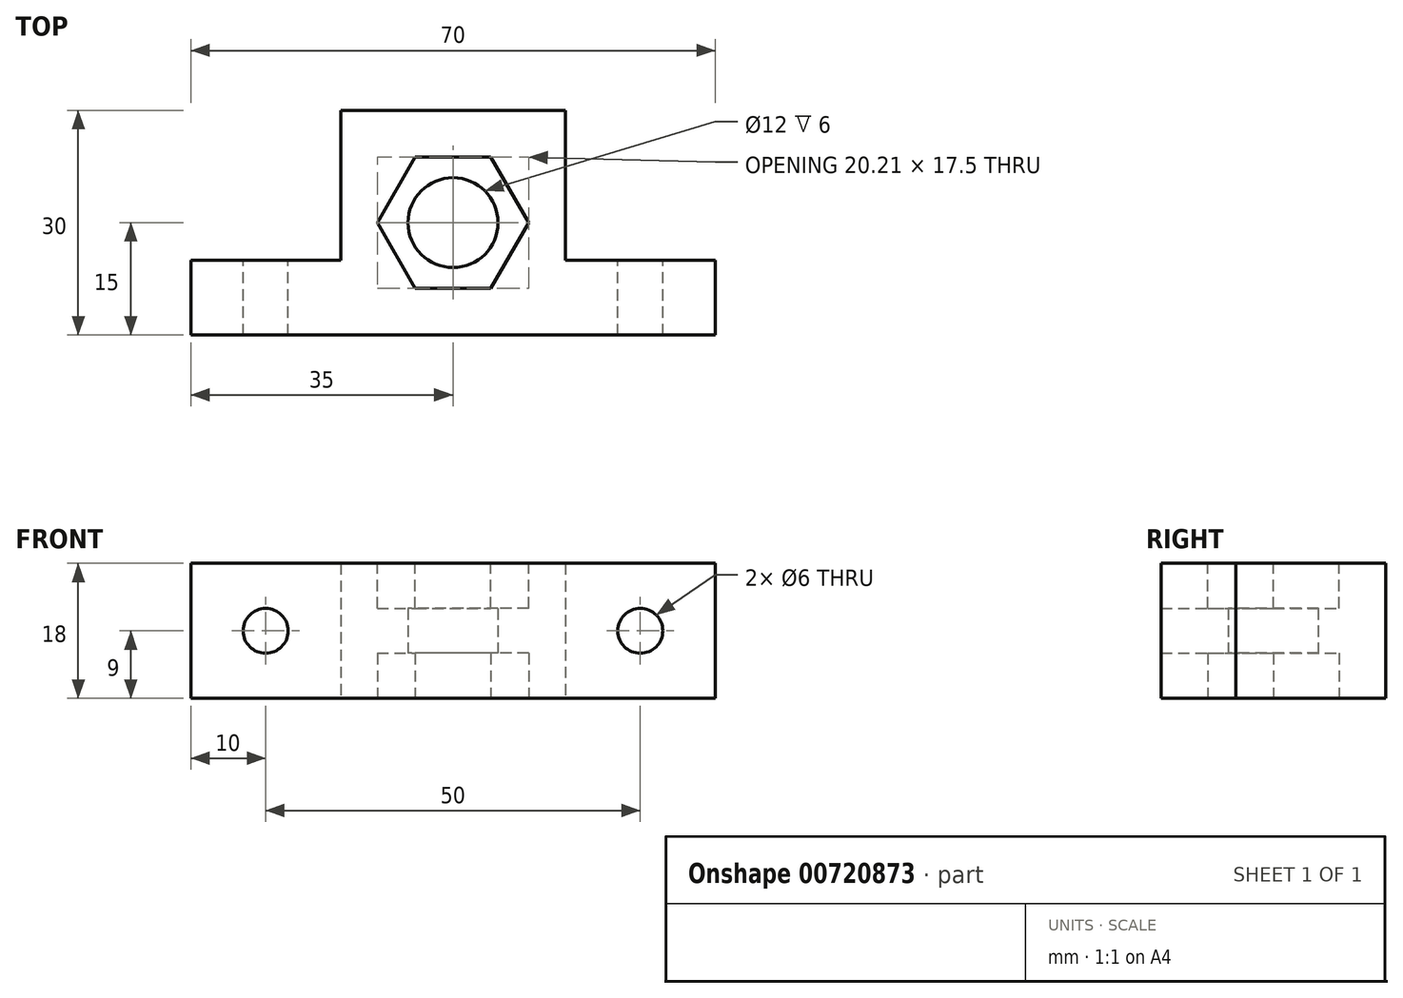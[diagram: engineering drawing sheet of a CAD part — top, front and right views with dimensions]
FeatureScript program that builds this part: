
annotation { "Feature Type Name" : "Feature", "Feature Type Description" : "" }
export const myFeature = defineFeature(function(context is Context, id is Id, definition is map)
    precondition{}
    {
        {
            var Q0;
            Q0=qCreatedBy(makeId("Top.planeOp"),FACE);
            var sketch = newSketch(context, id + "F0", { "sketchPlane" : qUnion([Q0])});
            skPoint(sketch, "E0.0", {"position": v(0, 0) * mm});
            skLineSegment(sketch, "E1.bottom", {"start": v(0, 0) * mm, "end": v(70, 0) * mm});
            skLineSegment(sketch, "E1.top", {"start": v(20, 30) * mm, "end": v(50, 30) * mm});
            skLineSegment(sketch, "E1.left", {"start": v(0, 0) * mm, "end": v(0, 10) * mm});
            skLineSegment(sketch, "E1.right", {"start": v(70, 0) * mm, "end": v(70, 10) * mm});
            skLineSegment(sketch, "E2.top", {"start": v(0, 10) * mm, "end": v(20, 10) * mm});
            skLineSegment(sketch, "E2.right", {"start": v(20, 30) * mm, "end": v(20, 10) * mm});
            skLineSegment(sketch, "E3.top", {"start": v(70, 10) * mm, "end": v(50, 10) * mm});
            skLineSegment(sketch, "E3.right", {"start": v(50, 30) * mm, "end": v(50, 10) * mm});
            skCircle(sketch, "E4", {"center": v(35, 15) * mm, "radius": 6 * mm});
            skPoint(sketch, "E4.centerSnap0", {"position": v(35, 0) * mm});
            skSolve(sketch);
        }
        {
            var Q0;
            Q0=makeQuery(id+"F0.imprint","IMPRINT",FACE,{"disambiguationData":[TD([[makeQuery(id+"F0.imprint","IMPRINT",EDGE,{"derivedFrom":sQuery(id+"F0.wireOp",EDGE,"E1.bottom")}),1.0]])]});
            extrude(context, id + "F1", {"entities" : qUnion([Q0]), "depth" : 18 * mm, "offsetDistance" : 25 * mm});
        }
        {
            var Q0;
            Q0=makeQuery(id+"F1.opExtrude","CAP_FACE",FACE,{"disambiguationData":[OSD([sQuery(id+"F0.wireOp",EDGE,"E1.bottom"),sQuery(id+"F0.wireOp",EDGE,"E1.top"),sQuery(id+"F0.wireOp",EDGE,"E1.left"),sQuery(id+"F0.wireOp",EDGE,"E1.right"),sQuery(id+"F0.wireOp",EDGE,"E2.top"),sQuery(id+"F0.wireOp",EDGE,"E2.right"),sQuery(id+"F0.wireOp",EDGE,"E3.top"),sQuery(id+"F0.wireOp",EDGE,"E3.right"),sQuery(id+"F0.wireOp",EDGE,"E4")])],"isStart":false});
            var sketch = newSketch(context, id + "F2", { "sketchPlane" : qUnion([Q0])});
            skCircle(sketch, "E5.cCircle", {"center": v(35, 15) * mm, "radius": 8.75 * mm, "construction": true});
            skLineSegment(sketch, "E5.0", {"start": v(29.95, 23.75) * mm, "end": v(40.05, 23.75) * mm});
            skLineSegment(sketch, "E5.1", {"start": v(40.05, 23.75) * mm, "end": v(45.1, 15) * mm});
            skLineSegment(sketch, "E5.2", {"start": v(45.1, 15) * mm, "end": v(40.05, 6.25) * mm});
            skLineSegment(sketch, "E5.3", {"start": v(40.05, 6.25) * mm, "end": v(29.95, 6.25) * mm});
            skLineSegment(sketch, "E5.4", {"start": v(29.95, 6.25) * mm, "end": v(24.9, 15) * mm});
            skLineSegment(sketch, "E5.5", {"start": v(24.9, 15) * mm, "end": v(29.95, 23.75) * mm});
            skPoint(sketch, "E5.0.midPoint", {"position": v(35, 23.75) * mm});
            skSolve(sketch);
        }
        {
            var Q0;
            Q0=makeQuery(id+"F2.imprint","IMPRINT",FACE,{"disambiguationData":[TD([[makeQuery(id+"F2.imprint","IMPRINT",EDGE,{"derivedFrom":sQuery(id+"F2.wireOp",EDGE,"E5.0")}),-1.0]])]});
            extrude(context, id + "F3", {"entities" : qUnion([Q0]), "operationType" : NewBodyOperationType.REMOVE, "oppositeDirection" : true, "depth" : 6 * mm, "offsetDistance" : 25 * mm});
        }
        {
            var Q0;
            Q0=makeQuery(id+"F1.opExtrude","SWEPT_FACE",FACE,{"disambiguationData":[OSD([sQuery(id+"F0.wireOp",EDGE,"E3.top")])]});
            var sketch = newSketch(context, id + "F4", { "sketchPlane" : qUnion([Q0])});
            skCircle(sketch, "E6", {"center": v(-60, 9) * mm, "radius": 3 * mm});
            skPoint(sketch, "E6.centerSnap0", {"position": v(-70, 9) * mm});
            skCircle(sketch, "E7", {"center": v(-10, 9) * mm, "radius": 3 * mm});
            skSolve(sketch);
        }
        {
            var Q0;
            Q0=makeQuery(id+"F4.imprint","IMPRINT",FACE,{"disambiguationData":[TD([[makeQuery(id+"F4.imprint","IMPRINT",EDGE,{"derivedFrom":sQuery(id+"F4.wireOp",EDGE,"E6")}),1.0]])]});
            var Q1;
            Q1=makeQuery(id+"F4.imprint","IMPRINT",FACE,{"disambiguationData":[TD([[makeQuery(id+"F4.imprint","IMPRINT",EDGE,{"derivedFrom":sQuery(id+"F4.wireOp",EDGE,"E7")}),1.0]])]});
            extrude(context, id + "F5", {"entities" : qUnion([Q0, Q1]), "operationType" : NewBodyOperationType.REMOVE, "oppositeDirection" : true, "depth" : 25 * mm, "offsetDistance" : 25 * mm});
        }
        {
            var Q0;
            Q0=makeQuery(id+"F1.opExtrude","CAP_FACE",FACE,{"disambiguationData":[OSD([sQuery(id+"F0.wireOp",EDGE,"E1.bottom"),sQuery(id+"F0.wireOp",EDGE,"E1.top"),sQuery(id+"F0.wireOp",EDGE,"E1.left"),sQuery(id+"F0.wireOp",EDGE,"E1.right"),sQuery(id+"F0.wireOp",EDGE,"E2.top"),sQuery(id+"F0.wireOp",EDGE,"E2.right"),sQuery(id+"F0.wireOp",EDGE,"E3.top"),sQuery(id+"F0.wireOp",EDGE,"E3.right"),sQuery(id+"F0.wireOp",EDGE,"E4")])],"isStart":true});
            var sketch = newSketch(context, id + "F6", { "sketchPlane" : qUnion([Q0])});
            skCircle(sketch, "E8.cCircle", {"center": v(35, -15) * mm, "radius": 8.75 * mm, "construction": true});
            skLineSegment(sketch, "E8.0", {"start": v(40.05, -23.75) * mm, "end": v(29.95, -23.75) * mm});
            skLineSegment(sketch, "E8.1", {"start": v(29.95, -23.75) * mm, "end": v(24.9, -15) * mm});
            skLineSegment(sketch, "E8.2", {"start": v(24.9, -15) * mm, "end": v(29.95, -6.25) * mm});
            skLineSegment(sketch, "E8.3", {"start": v(29.95, -6.25) * mm, "end": v(40.05, -6.25) * mm});
            skLineSegment(sketch, "E8.4", {"start": v(40.05, -6.25) * mm, "end": v(45.1, -15) * mm});
            skLineSegment(sketch, "E8.5", {"start": v(45.1, -15) * mm, "end": v(40.05, -23.75) * mm});
            skPoint(sketch, "E8.0.midPoint", {"position": v(35, -23.75) * mm});
            skSolve(sketch);
        }
        {
            var Q0;
            Q0=makeQuery(id+"F6.imprint","IMPRINT",FACE,{"disambiguationData":[TD([[makeQuery(id+"F6.imprint","IMPRINT",EDGE,{"derivedFrom":sQuery(id+"F6.wireOp",EDGE,"E8.0")}),-1.0]])]});
            extrude(context, id + "F7", {"entities" : qUnion([Q0]), "operationType" : NewBodyOperationType.REMOVE, "oppositeDirection" : true, "depth" : 6 * mm, "offsetDistance" : 25 * mm});
        }
    });
